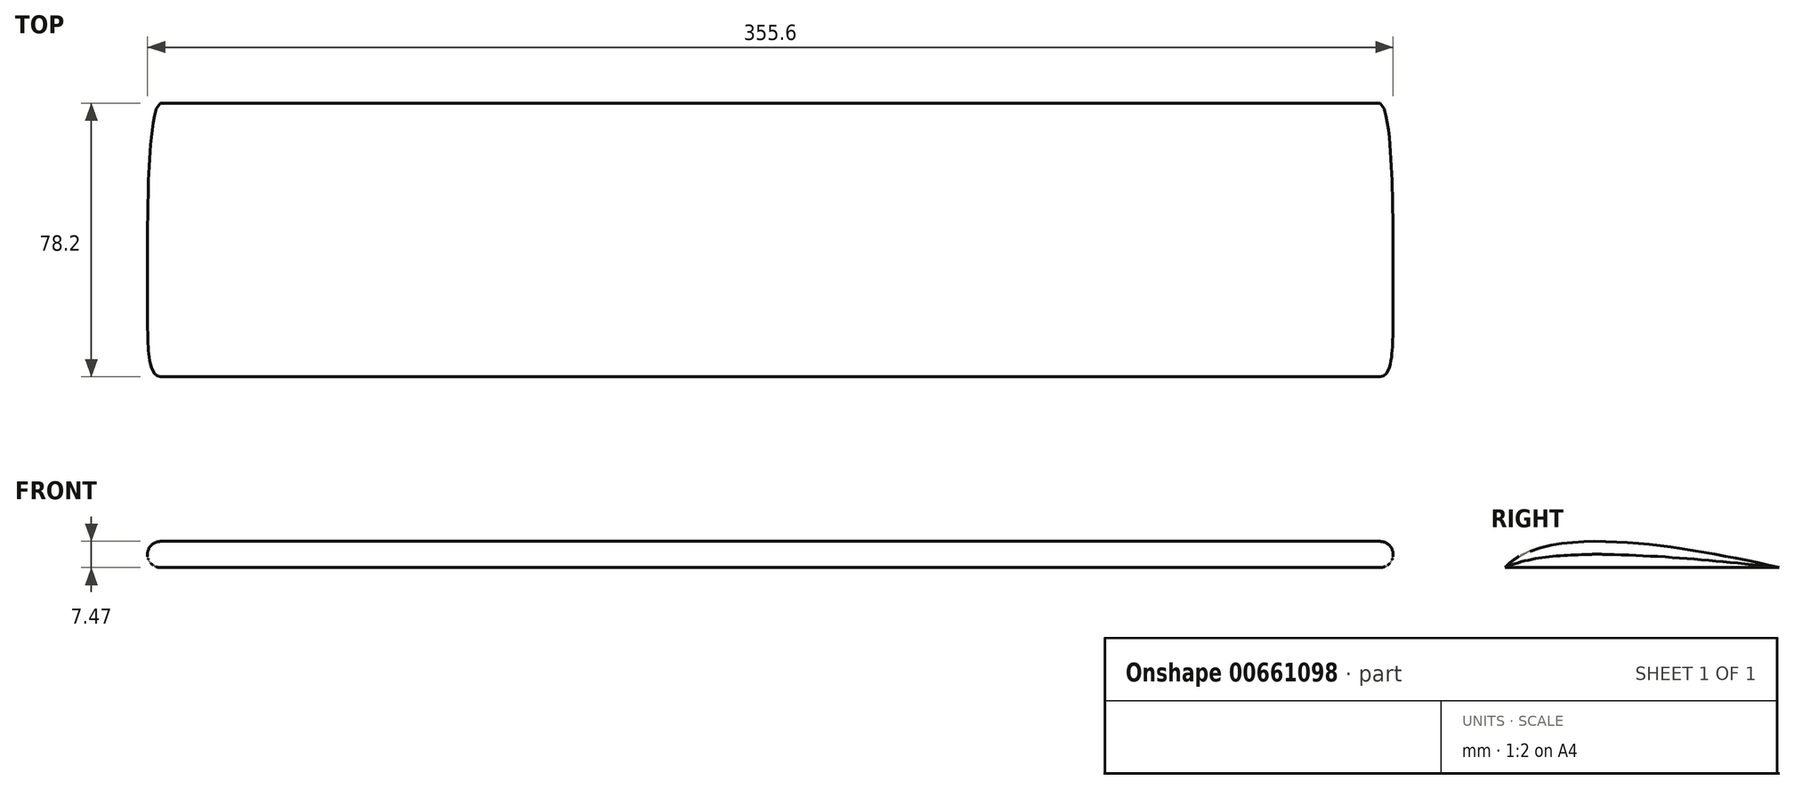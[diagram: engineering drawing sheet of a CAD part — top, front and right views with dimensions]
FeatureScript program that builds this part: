
annotation { "Feature Type Name" : "Feature", "Feature Type Description" : "" }
export const myFeature = defineFeature(function(context is Context, id is Id, definition is map)
    precondition{}
    {
        {
            var Q0;
            Q0=qCreatedBy(makeId("Right.planeOp"),FACE);
            var sketch = newSketch(context, id + "F0", { "sketchPlane" : qUnion([Q0])});
            skLineSegment(sketch, "E0", {"start": v(-39.85, 0) * mm, "end": v(38.35, 0) * mm});
            skFitSpline(sketch, "E1", {"points": [v(-39.85, 0) * mm, v(38.35, 0) * mm], "startDerivative": vector(33.39, 37.45) * mm, "endDerivative": vector(92.04, -21.2) * mm});
            skSolve(sketch);
        }
        {
            var Q0;
            Q0 = qSketchRegion(id + "F0", true);
            extrude(context, id + "F1", {"entities" : qUnion([Q0]), "endBound" : BoundingType.SYMMETRIC, "depth" : 355.6 * mm, "offsetDistance" : 25.4 * mm});
        }
        {
            var Q0;
            Q0=makeQuery(id+"F1.opExtrude","CAP_EDGE",EDGE,{"disambiguationData":[OSD([sQuery(id+"F0.wireOp",EDGE,"E1")])],"isStart":false});
            var Q1;
            Q1=makeQuery(id+"F1.opExtrude","CAP_EDGE",EDGE,{"disambiguationData":[OSD([sQuery(id+"F0.wireOp",EDGE,"E0")])],"isStart":false});
            var Q2;
            Q2=makeQuery(id+"F1.opExtrude","CAP_EDGE",EDGE,{"disambiguationData":[OSD([sQuery(id+"F0.wireOp",EDGE,"E1")])],"isStart":true});
            var Q3;
            Q3=makeQuery(id+"F1.opExtrude","CAP_EDGE",EDGE,{"disambiguationData":[OSD([sQuery(id+"F0.wireOp",EDGE,"E0")])],"isStart":true});
            fillet(context, id + "F2", {"entities" : qUnion([Q0, Q1, Q2, Q3]), "radius" : 3.68 * mm, "tangentPropagation" : true, "allowEdgeOverflow" : false});
        }
    });
